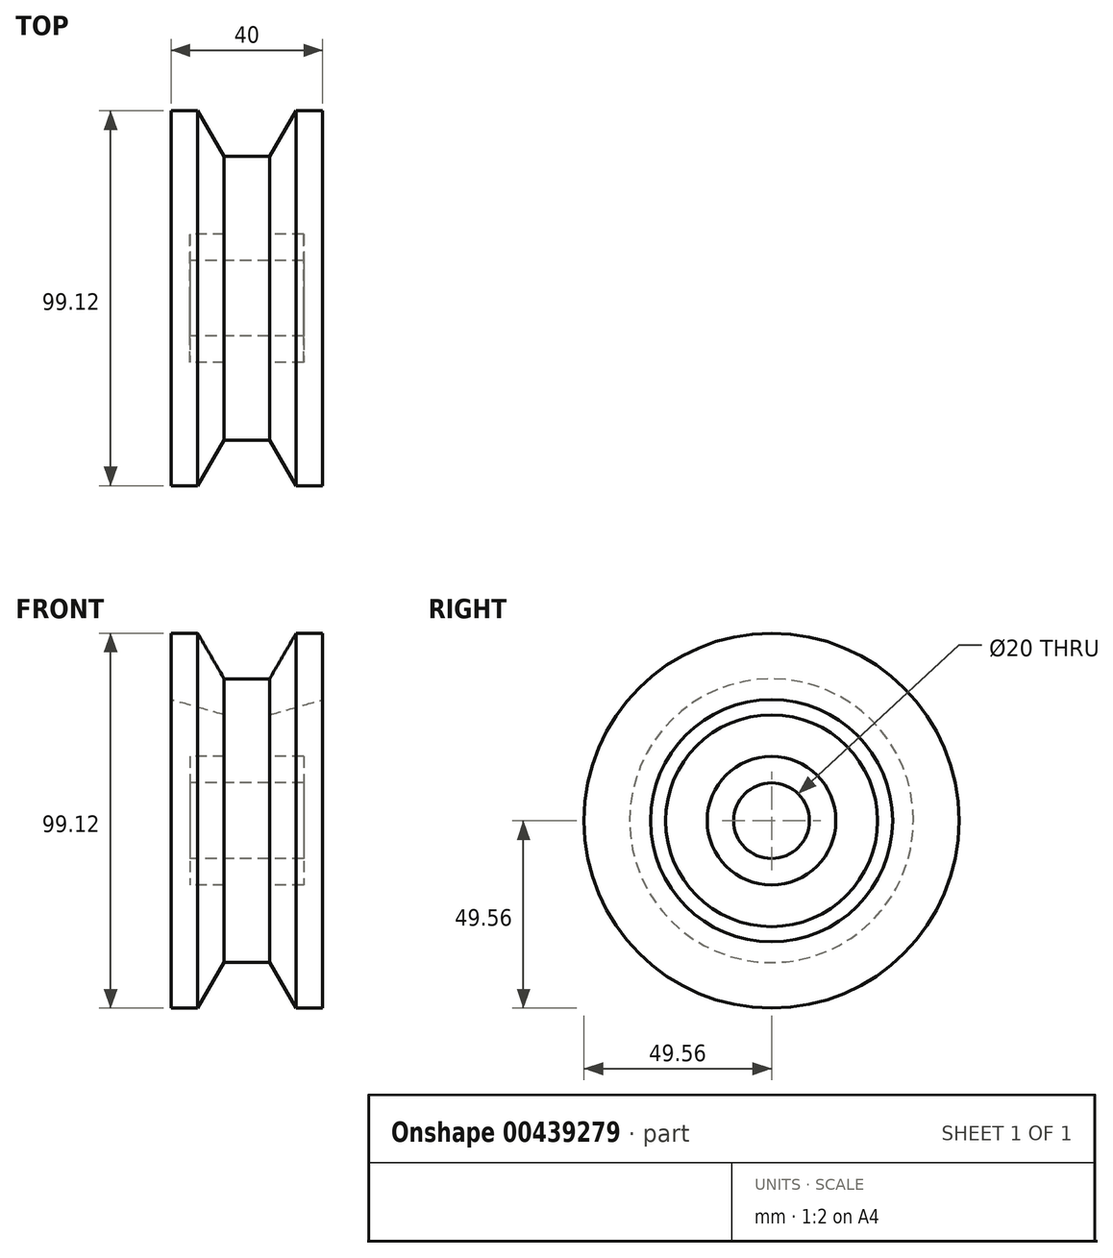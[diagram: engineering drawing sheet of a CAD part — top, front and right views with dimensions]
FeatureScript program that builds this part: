
annotation { "Feature Type Name" : "Feature", "Feature Type Description" : "" }
export const myFeature = defineFeature(function(context is Context, id is Id, definition is map)
    precondition{}
    {
        {
            var Q0;
            Q0=qCreatedBy(makeId("Front.planeOp"),FACE);
            var sketch = newSketch(context, id + "F0", { "sketchPlane" : qUnion([Q0])});
            skLineSegment(sketch, "E0", {"start": v(-15, -10) * mm, "end": v(15, -10) * mm});
            skPoint(sketch, "E1", {"position": v(0, -10) * mm});
            skLineSegment(sketch, "E2", {"start": v(15, -10) * mm, "end": v(15, -17) * mm});
            skLineSegment(sketch, "E3", {"start": v(15, -17) * mm, "end": v(6, -17) * mm});
            skLineSegment(sketch, "E4", {"start": v(6, -17) * mm, "end": v(6, -28) * mm});
            skLineSegment(sketch, "E5.MirrorCS", {"start": v(15, -10) * mm, "end": v(-15, -10) * mm});
            skLineSegment(sketch, "E6.MirrorCS", {"start": v(-15, -10) * mm, "end": v(-15, -17) * mm});
            skLineSegment(sketch, "E7.MirrorCS", {"start": v(-6, -17) * mm, "end": v(-6, -28) * mm});
            skLineSegment(sketch, "E8.MirrorCS", {"start": v(-15, -17) * mm, "end": v(-6, -17) * mm});
            skLineSegment(sketch, "E9", {"start": v(6, -28) * mm, "end": v(20, -32) * mm});
            skLineSegment(sketch, "E10.MirrorCS", {"start": v(-6, -28) * mm, "end": v(-20, -32) * mm});
            skLineSegment(sketch, "E11", {"start": v(20, -32) * mm, "end": v(20, -49.56) * mm});
            skLineSegment(sketch, "E12", {"start": v(20, -49.56) * mm, "end": v(13, -49.56) * mm});
            skLineSegment(sketch, "E13", {"start": v(13, -49.56) * mm, "end": v(6, -37.5) * mm});
            skLineSegment(sketch, "E14", {"start": v(6, -37.5) * mm, "end": v(-6, -37.5) * mm});
            skLineSegment(sketch, "E15.MirrorCS", {"start": v(-13, -49.56) * mm, "end": v(-6, -37.5) * mm});
            skLineSegment(sketch, "E16.MirrorCS", {"start": v(-20, -49.56) * mm, "end": v(-13, -49.56) * mm});
            skLineSegment(sketch, "E17.MirrorCS", {"start": v(-20, -32) * mm, "end": v(-20, -49.56) * mm});
            skLineSegment(sketch, "E18", {"start": v(0, 0) * mm, "end": v(7.5, 0) * mm});
            skSolve(sketch);
        }
        {
            var Q0;
            Q0=makeQuery(id+"F0.imprint","IMPRINT",FACE,{"disambiguationData":[TD([[makeQuery(id+"F0.imprint","IMPRINT",EDGE,{"derivedFrom":sQuery(id+"F0.wireOp",EDGE,"E2")}),-1.0]])]});
            var Q1;
            Q1=sQuery(id+"F0.wireOp",EDGE,"E18");
            revolve(context, id + "F1", {"entities" : qUnion([Q0]), "axis" : qUnion([Q1]), "revolveType" : RevolveType.FULL});
        }
    });
